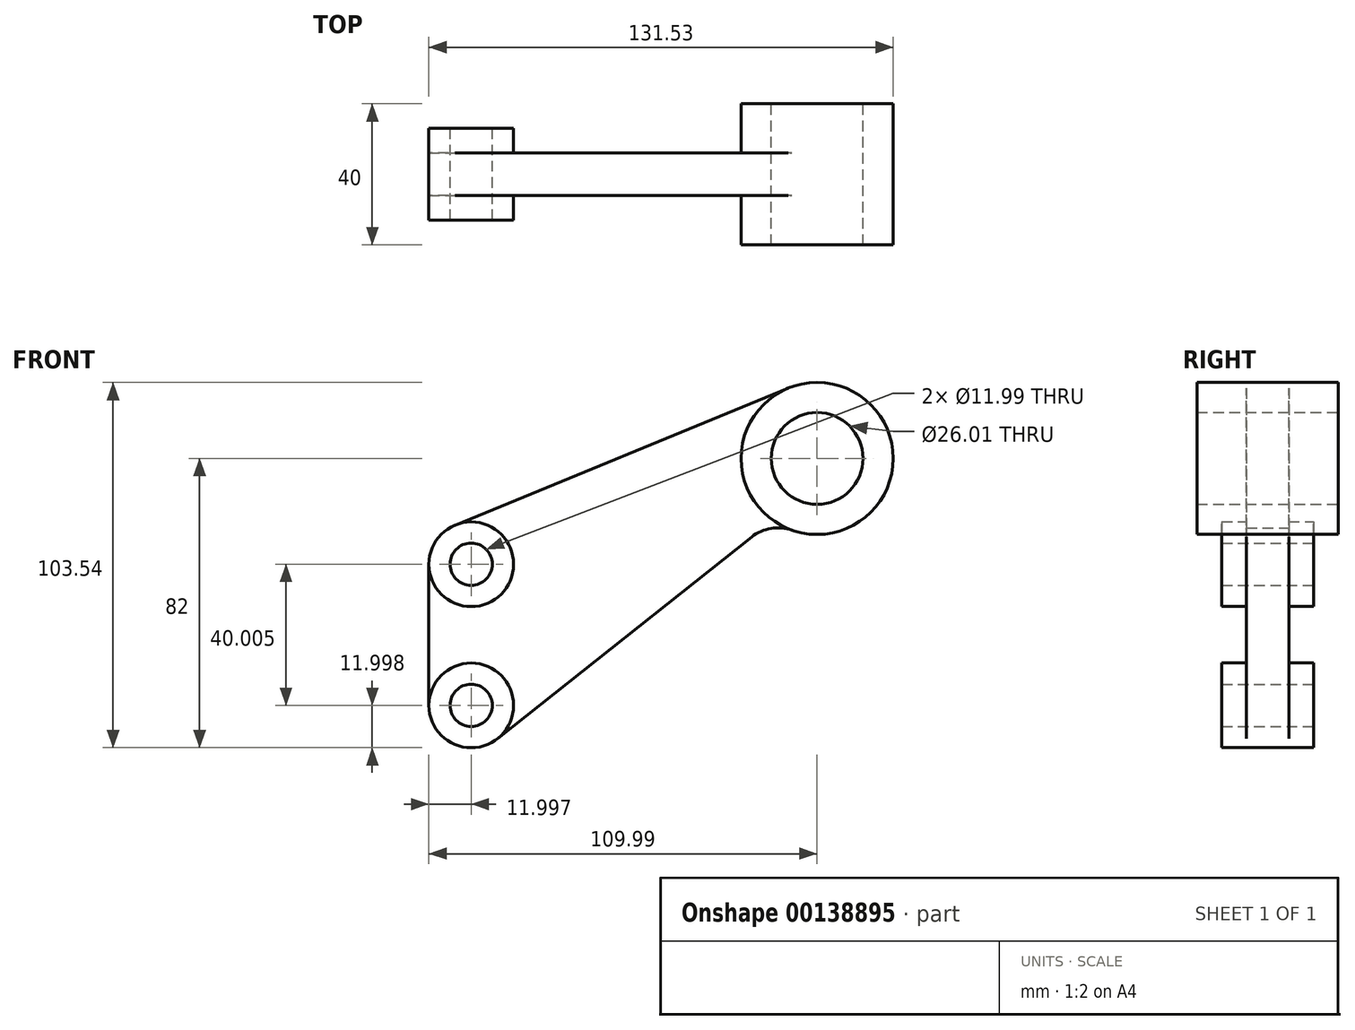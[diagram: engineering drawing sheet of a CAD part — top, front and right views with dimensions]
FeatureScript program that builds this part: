
annotation { "Feature Type Name" : "Feature", "Feature Type Description" : "" }
export const myFeature = defineFeature(function(context is Context, id is Id, definition is map)
    precondition{}
    {
        {
            var Q0;
            Q0=qCreatedBy(makeId("Front.planeOp"),FACE);
            var sketch = newSketch(context, id + "F0", { "sketchPlane" : qUnion([Q0])});
            skCircle(sketch, "E0", {"center": v(0, 0) * mm, "radius": 13 * mm});
            skCircle(sketch, "E1", {"center": v(0, 0) * mm, "radius": 21.54 * mm});
            skCircle(sketch, "E2", {"center": v(-98, -30) * mm, "radius": 12 * mm});
            skCircle(sketch, "E3", {"center": v(-98, -70) * mm, "radius": 12 * mm});
            skLineSegment(sketch, "E4", {"start": v(-102.56, -18.9) * mm, "end": v(-8.2, 19.92) * mm});
            skLineSegment(sketch, "E5", {"start": v(-110, -30) * mm, "end": v(-110, -70) * mm});
            skCircle(sketch, "E6", {"center": v(-98, -30) * mm, "radius": 6 * mm});
            skCircle(sketch, "E7", {"center": v(-98, -70) * mm, "radius": 6 * mm});
            skLineSegment(sketch, "E8", {"start": v(-90.53, -79.4) * mm, "end": v(-18.52, -22.26) * mm});
            skArc(sketch, "E9", {"start": v(-7.11, -20.33) * mm, "mid": v(-13.06, -19.83) * mm, "end": v(-18.52, -22.26) * mm});
            skSolve(sketch);
        }
        {
            var Q0;
            Q0=makeQuery(id+"F0.imprint","IMPRINT",FACE,{"disambiguationData":[TD([[makeQuery(id+"F0.imprint","IMPRINT",EDGE,{"derivedFrom":sQuery(id+"F0.wireOp",EDGE,"E0")}),-1.0]])]});
            extrude(context, id + "F1", {"entities" : qUnion([Q0]), "endBound" : BoundingType.SYMMETRIC, "depth" : 40 * mm});
        }
        {
            var Q0;
            {var subQ0=sQuery(id+"F0.wireOp",EDGE,"E4");Q0=makeQuery(id+"F0.imprint","IMPRINT",FACE,{"disambiguationData":[TD([[makeQuery(id+"F0.imprint","IMPRINT",EDGE,{"derivedFrom":subQ0}),-1.0]])]});}
            extrude(context, id + "F2", {"entities" : qUnion([Q0]), "operationType" : NewBodyOperationType.ADD, "endBound" : BoundingType.SYMMETRIC, "depth" : 12 * mm});
        }
        {
            var Q0;
            Q0=makeQuery(id+"F0.imprint","IMPRINT",FACE,{"disambiguationData":[TD([[makeQuery(id+"F0.imprint","IMPRINT",EDGE,{"derivedFrom":sQuery(id+"F0.wireOp",EDGE,"E7")}),-1.0]])]});
            var Q1;
            Q1=makeQuery(id+"F0.imprint","IMPRINT",FACE,{"disambiguationData":[TD([[makeQuery(id+"F0.imprint","IMPRINT",EDGE,{"derivedFrom":sQuery(id+"F0.wireOp",EDGE,"E6")}),-1.0]])]});
            extrude(context, id + "F3", {"entities" : qUnion([Q0, Q1]), "operationType" : NewBodyOperationType.ADD, "endBound" : BoundingType.SYMMETRIC, "depth" : 26 * mm});
        }
    });
